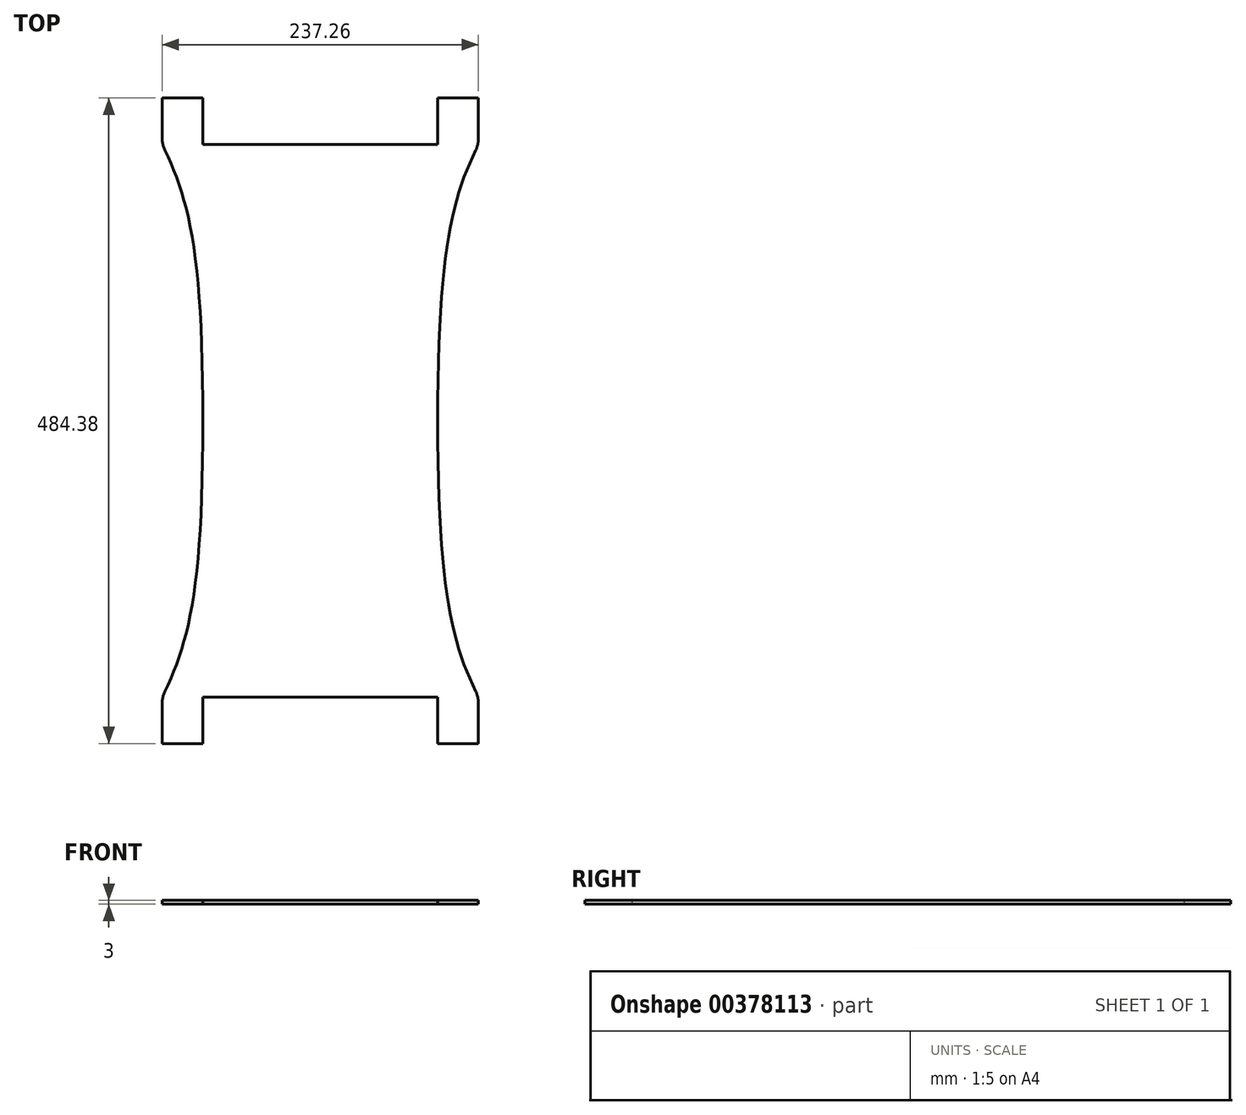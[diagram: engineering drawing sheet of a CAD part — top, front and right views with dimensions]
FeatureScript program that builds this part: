
annotation { "Feature Type Name" : "Feature", "Feature Type Description" : "" }
export const myFeature = defineFeature(function(context is Context, id is Id, definition is map)
    precondition{}
    {
        {
            var Q0;
            Q0=qCreatedBy(makeId("Top.planeOp"),FACE);
            var sketch = newSketch(context, id + "F0", { "sketchPlane" : qUnion([Q0])});
            skLineSegment(sketch, "E0.top", {"start": v(-88.13, -207.19) * mm, "end": v(0, -207.19) * mm});
            skLineSegment(sketch, "E1.right", {"start": v(-118.63, -211.83) * mm, "end": v(-118.63, -242.19) * mm});
            skLineSegment(sketch, "E2", {"start": v(-88.13, -207.19) * mm, "end": v(-88.13, -242.19) * mm});
            skLineSegment(sketch, "E3.trimOffspring", {"start": v(-88.13, -242.19) * mm, "end": v(-118.63, -242.19) * mm});
            skLineSegment(sketch, "E4", {"start": v(0, 0) * mm, "end": v(-154.45, 0) * mm, "construction": true});
            skFitSpline(sketch, "E5", {"points": [v(-88.13, 0) * mm, v(-118.63, -207.19) * mm, v(-166.62, -276.29) * mm], "startDerivative": vector(0, -631.8) * mm, "endDerivative": vector(-155.15, -155.15) * mm});
            skLineSegment(sketch, "E6.trimOffspring", {"start": v(0, -207.19) * mm, "end": v(-88.13, -207.19) * mm});
            skPoint(sketch, "E0.bottom.start.orphan", {"position": v(-88.13, 207.19) * mm});
            skLineSegment(sketch, "E7", {"start": v(0, 0) * mm, "end": v(0, 86.17) * mm, "construction": true});
            skArc(sketch, "E8.filletArc", {"start": v(-116.64, -203.14) * mm, "mid": v(-118.13, -207.37) * mm, "end": v(-118.63, -211.83) * mm});
            skLineSegment(sketch, "E9.MirrorCS", {"start": v(88.13, -242.19) * mm, "end": v(118.63, -242.19) * mm});
            skLineSegment(sketch, "E10.MirrorCS", {"start": v(0, -207.19) * mm, "end": v(88.13, -207.19) * mm});
            skLineSegment(sketch, "E11.MirrorCS", {"start": v(118.63, -211.83) * mm, "end": v(118.63, -242.19) * mm});
            skLineSegment(sketch, "E12.MirrorCS", {"start": v(88.13, -207.19) * mm, "end": v(88.13, -242.19) * mm});
            skArc(sketch, "E13.MirrorCS", {"start": v(116.64, -203.14) * mm, "mid": v(118.13, -207.37) * mm, "end": v(118.63, -211.83) * mm});
            skFitSpline(sketch, "E14.MirrorCS", {"points": [v(88.13, 0) * mm, v(118.63, -207.19) * mm, v(166.62, -276.29) * mm], "startDerivative": vector(0, -631.8) * mm, "endDerivative": vector(155.15, -155.15) * mm});
            skArc(sketch, "E15.MirrorCS", {"start": v(116.64, 203.14) * mm, "mid": v(118.13, 207.37) * mm, "end": v(118.63, 211.83) * mm});
            skArc(sketch, "E16.MirrorCS", {"start": v(-116.64, 203.14) * mm, "mid": v(-118.13, 207.37) * mm, "end": v(-118.63, 211.83) * mm});
            skLineSegment(sketch, "E17.MirrorCS", {"start": v(-88.13, 207.19) * mm, "end": v(0, 207.19) * mm});
            skFitSpline(sketch, "E18.MirrorCS", {"points": [v(-88.13, 0) * mm, v(-118.63, 207.19) * mm, v(-166.62, 276.29) * mm], "startDerivative": vector(0, 631.8) * mm, "endDerivative": vector(-155.15, 155.15) * mm});
            skLineSegment(sketch, "E19.MirrorCS", {"start": v(-118.63, 211.83) * mm, "end": v(-118.63, 242.19) * mm});
            skFitSpline(sketch, "E20.MirrorCS", {"points": [v(88.13, 0) * mm, v(118.63, 207.19) * mm, v(166.62, 276.29) * mm], "startDerivative": vector(0, 631.8) * mm, "endDerivative": vector(155.15, 155.15) * mm});
            skLineSegment(sketch, "E21.MirrorCS", {"start": v(0, 207.19) * mm, "end": v(88.14, 207.19) * mm});
            skLineSegment(sketch, "E22.MirrorCS", {"start": v(88.14, 242.19) * mm, "end": v(118.63, 242.19) * mm});
            skLineSegment(sketch, "E23.MirrorCS", {"start": v(-88.13, 207.19) * mm, "end": v(-88.13, 242.19) * mm});
            skLineSegment(sketch, "E24.MirrorCS", {"start": v(88.14, 207.19) * mm, "end": v(88.14, 242.19) * mm});
            skLineSegment(sketch, "E25.MirrorCS", {"start": v(118.63, 211.83) * mm, "end": v(118.63, 242.19) * mm});
            skLineSegment(sketch, "E26.MirrorCS", {"start": v(0, 207.19) * mm, "end": v(-88.13, 207.19) * mm});
            skLineSegment(sketch, "E27.MirrorCS", {"start": v(-88.13, 242.19) * mm, "end": v(-118.63, 242.19) * mm});
            skSolve(sketch);
        }
        {
            var Q0;
            Q0 = qSketchRegion(id + "F0", true);
            extrude(context, id + "F1", {"entities" : qUnion([Q0]), "depth" : 3 * mm});
        }
    });
